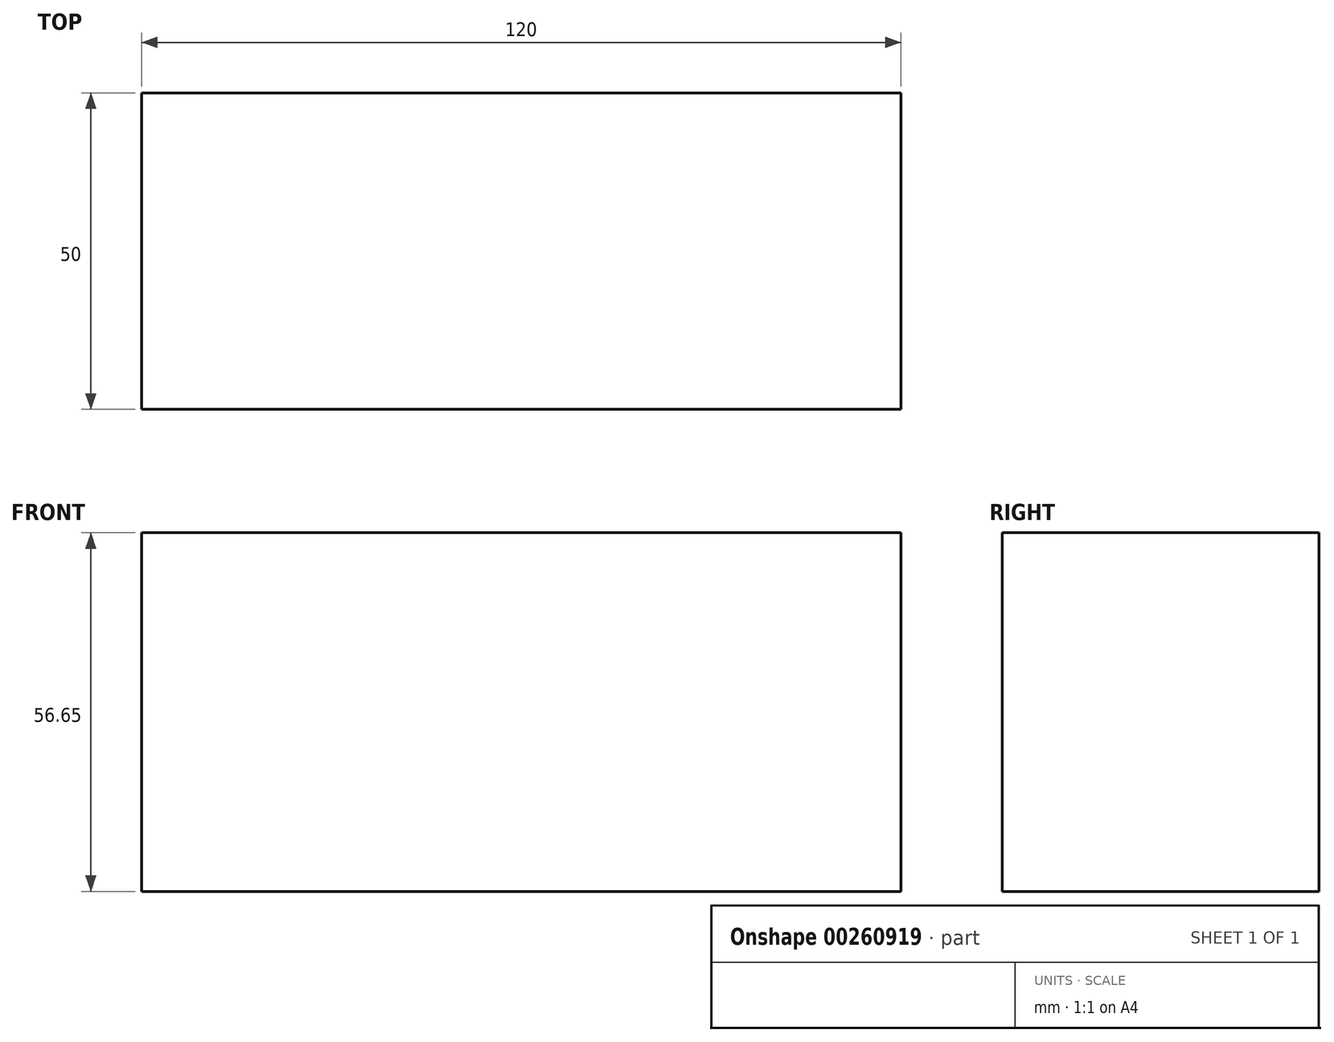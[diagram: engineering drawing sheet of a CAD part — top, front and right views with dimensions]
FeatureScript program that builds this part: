
annotation { "Feature Type Name" : "Feature", "Feature Type Description" : "" }
export const myFeature = defineFeature(function(context is Context, id is Id, definition is map)
    precondition{}
    {
        {
            var Q0;
            Q0=qCreatedBy(makeId("Front.planeOp"),FACE);
            var sketch = newSketch(context, id + "F0", { "sketchPlane" : qUnion([Q0])});
            skLineSegment(sketch, "E0", {"start": v(-84.25, 0) * mm, "end": v(35.75, 0) * mm});
            skLineSegment(sketch, "E1", {"start": v(-84.25, 0) * mm, "end": v(-84.25, 56.65) * mm});
            skLineSegment(sketch, "E2", {"start": v(-84.25, 56.65) * mm, "end": v(35.75, 56.65) * mm});
            skLineSegment(sketch, "E3", {"start": v(35.75, 56.65) * mm, "end": v(35.75, 0) * mm});
            skSolve(sketch);
        }
        {
            var Q0;
            Q0=makeQuery(id+"F0.imprint","IMPRINT",FACE,{"disambiguationData":[TD([[makeQuery(id+"F0.imprint","IMPRINT",EDGE,{"derivedFrom":sQuery(id+"F0.wireOp",EDGE,"E0")}),1.0]])]});
            extrude(context, id + "F1", {"entities" : qUnion([Q0]), "endBound" : BoundingType.SYMMETRIC, "depth" : 50 * mm});
        }
    });
